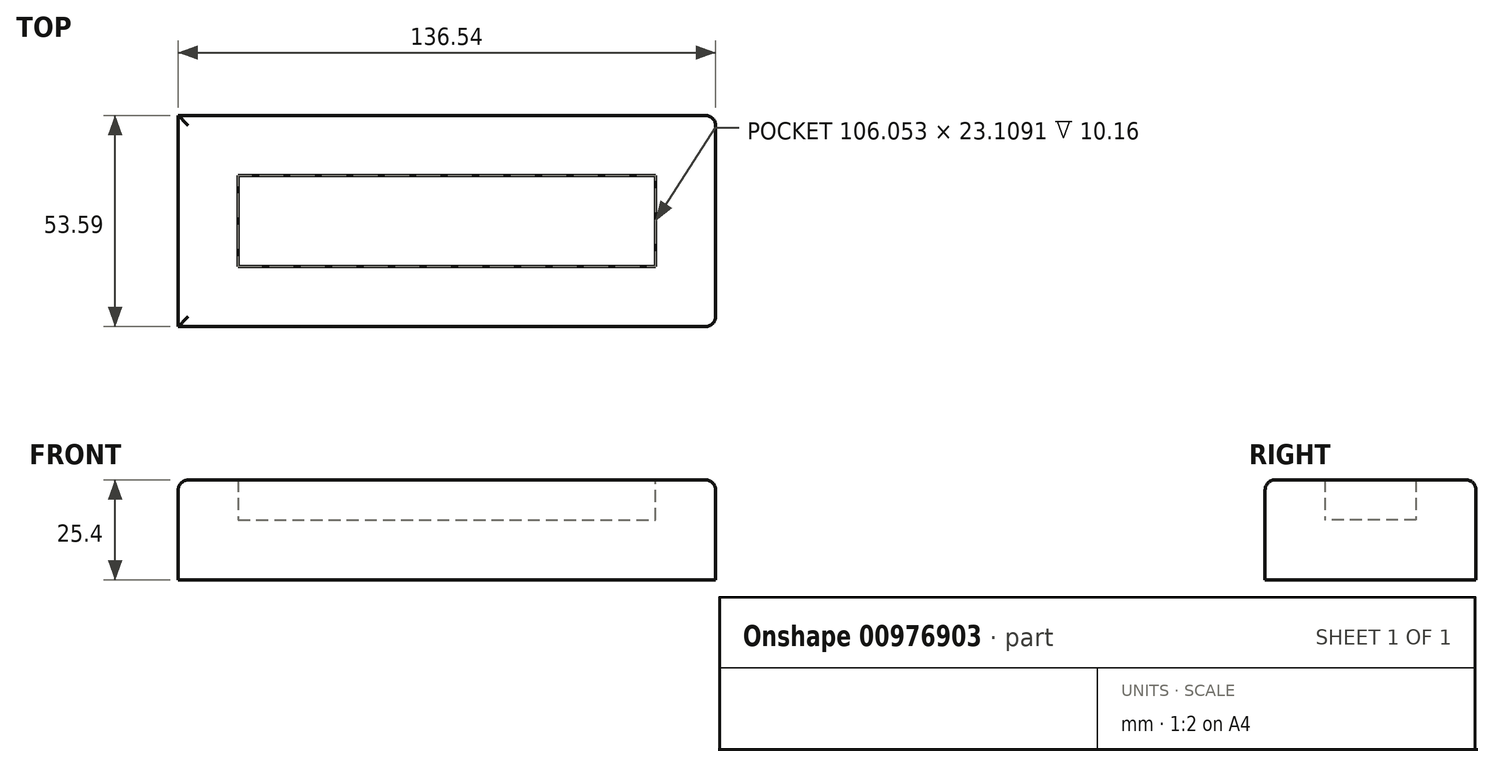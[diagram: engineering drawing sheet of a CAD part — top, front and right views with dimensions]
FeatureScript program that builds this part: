
annotation { "Feature Type Name" : "Feature", "Feature Type Description" : "" }
export const myFeature = defineFeature(function(context is Context, id is Id, definition is map)
    precondition{}
    {
        {
            var Q0;
            Q0=qCreatedBy(makeId("Top.planeOp"),FACE);
            var sketch = newSketch(context, id + "F0", { "sketchPlane" : qUnion([Q0])});
            skLineSegment(sketch, "E0.bottom", {"start": v(-104.16, -13.96) * mm, "end": v(32.38, -13.96) * mm});
            skLineSegment(sketch, "E0.top", {"start": v(-104.16, -67.55) * mm, "end": v(32.38, -67.55) * mm});
            skLineSegment(sketch, "E0.left", {"start": v(-104.16, -13.96) * mm, "end": v(-104.16, -67.55) * mm});
            skLineSegment(sketch, "E0.right", {"start": v(32.38, -13.96) * mm, "end": v(32.38, -67.55) * mm});
            skSolve(sketch);
        }
        {
            var Q0;
            Q0 = qSketchRegion(id + "F0", true);
            var Q1;
            Q1=makeQuery(id+"F0.imprint","IMPRINT",FACE,{"disambiguationData":[TD([[makeQuery(id+"F0.imprint","IMPRINT",EDGE,{"derivedFrom":sQuery(id+"F0.wireOp",EDGE,"E0.bottom")}),-1.0]])]});
            extrude(context, id + "F1", {"entities" : qUnion([Q0, Q1]), "depth" : 25.4 * mm, "offsetDistance" : 25.4 * mm});
        }
        {
            var Q0;
            Q0=makeQuery(id+"F1.opExtrude","CAP_FACE",FACE,{"disambiguationData":[OSD([sQuery(id+"F0.wireOp",EDGE,"E0.bottom"),sQuery(id+"F0.wireOp",EDGE,"E0.top"),sQuery(id+"F0.wireOp",EDGE,"E0.left"),sQuery(id+"F0.wireOp",EDGE,"E0.right")])],"isStart":false});
            var Q1;
            Q1=makeQuery(id+"F1.opExtrude","CAP_EDGE",EDGE,{"disambiguationData":[OSD([sQuery(id+"F0.wireOp",EDGE,"E0.top")])],"isStart":false});
            var Q2;
            Q2=makeQuery(id+"F1.opExtrude","SWEPT_EDGE",EDGE,{"disambiguationData":[OSD([sQuery(id+"F0.wireOp",EDGE,"E0.top"),sQuery(id+"F0.wireOp",EDGE,"E0.right")])]});
            var Q3;
            Q3=makeQuery(id+"F1.opExtrude","SWEPT_EDGE",EDGE,{"disambiguationData":[OSD([sQuery(id+"F0.wireOp",EDGE,"E0.bottom"),sQuery(id+"F0.wireOp",EDGE,"E0.right")])]});
            fillet(context, id + "F2", {"entities" : qUnion([Q0, Q1, Q2, Q3]), "radius" : 2.54 * mm, "tangentPropagation" : true, "allowEdgeOverflow" : false});
        }
        {
            var Q0;
            Q0=makeQuery(id+"F1.opExtrude","CAP_FACE",FACE,{"disambiguationData":[OSD([sQuery(id+"F0.wireOp",EDGE,"E0.bottom"),sQuery(id+"F0.wireOp",EDGE,"E0.top"),sQuery(id+"F0.wireOp",EDGE,"E0.left"),sQuery(id+"F0.wireOp",EDGE,"E0.right")])],"isStart":false});
            shell(context, id + "F3", {"entities" : qUnion([Q0]), "thickness" : 15.24 * mm});
        }
    });
